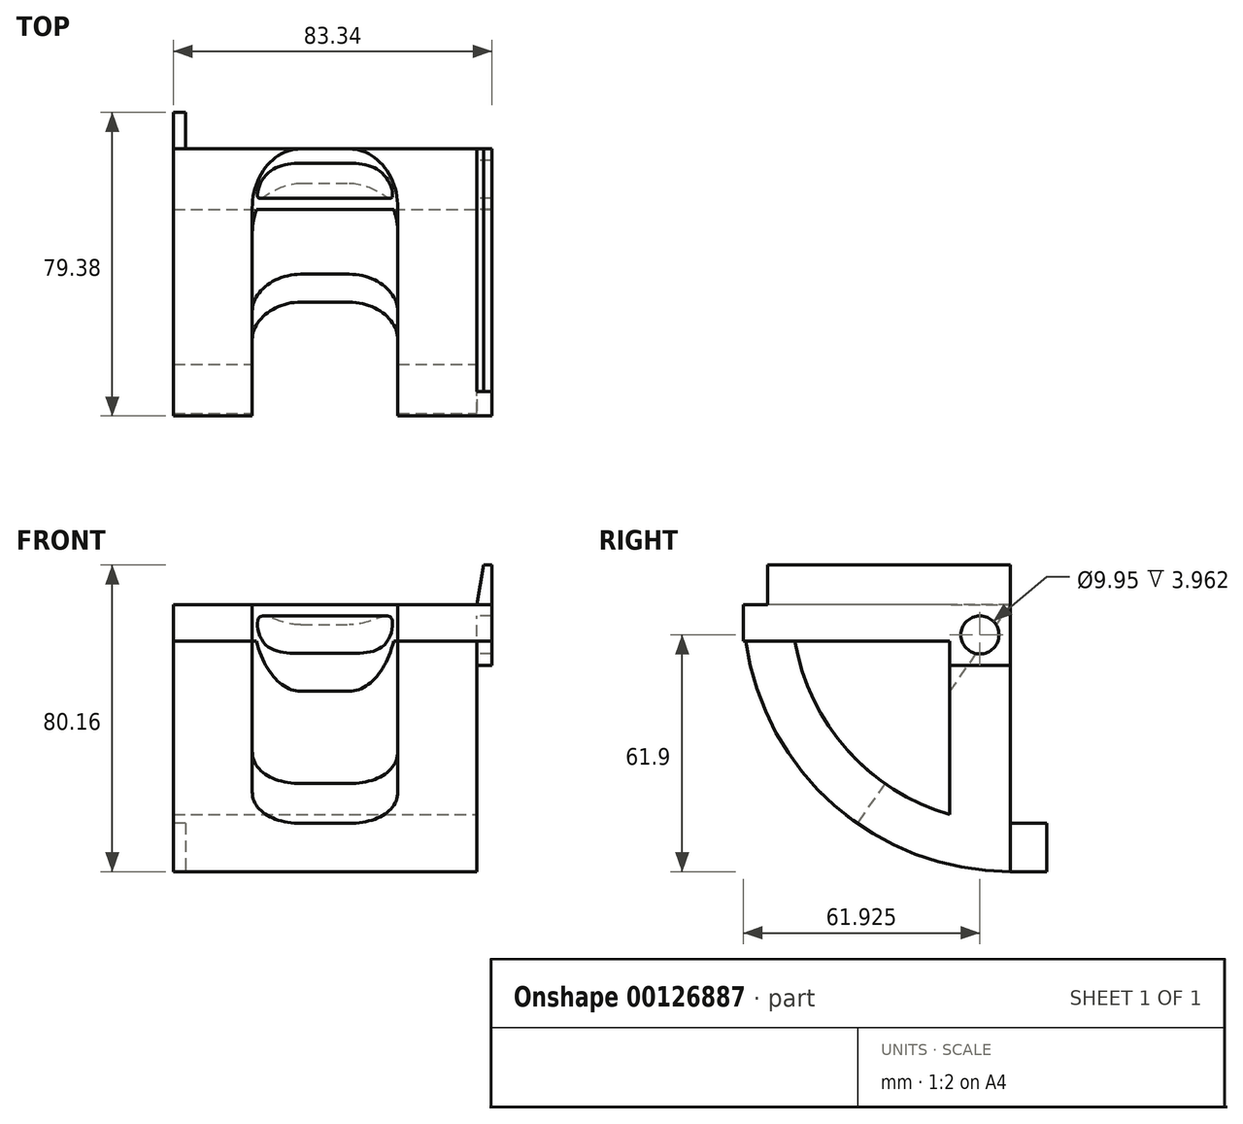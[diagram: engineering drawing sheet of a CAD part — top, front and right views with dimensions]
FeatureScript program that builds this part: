
annotation { "Feature Type Name" : "Feature", "Feature Type Description" : "" }
export const myFeature = defineFeature(function(context is Context, id is Id, definition is map)
    precondition{}
    {
        {
            var Q0;
            Q0=qCreatedBy(makeId("Right.planeOp"),FACE);
            var sketch = newSketch(context, id + "F0", { "sketchPlane" : qUnion([Q0])});
            skLineSegment(sketch, "E0.bottom", {"start": v(0, 0) * mm, "end": v(-69.85, 0) * mm});
            skLineSegment(sketch, "E0.left", {"start": v(0, 0) * mm, "end": v(0, -69.85) * mm});
            skLineSegment(sketch, "E0.right", {"start": v(-69.85, 0) * mm, "end": v(-69.85, -9.53) * mm});
            skArc(sketch, "E1", {"start": v(-57.15, 0) * mm, "mid": v(-40.41, -40.41) * mm, "end": v(0, -57.15) * mm});
            skArc(sketch, "E2", {"start": v(-69.85, 0) * mm, "mid": v(-49.4, -49.4) * mm, "end": v(0, -69.85) * mm});
            skLineSegment(sketch, "E3.0", {"start": v(0, -9.52) * mm, "end": v(-69.85, -9.53) * mm});
            skLineSegment(sketch, "E4.0", {"start": v(-15.87, -9.52) * mm, "end": v(-15.87, -54.9) * mm});
            skSolve(sketch);
        }
        {
            var Q0;
            Q0 = qSketchRegion(id + "F0", true);
            extrude(context, id + "F1", {"entities" : qUnion([Q0]), "oppositeDirection" : true, "depth" : 79.38 * mm});
        }
        {
            var Q0;
            Q0=qCreatedBy(makeId("Right.planeOp"),FACE);
            cPlane(context, id + "F2", {"entities" : qUnion([Q0]), "cplaneType" : CPlaneType.OFFSET, "offset" : 39.69 * mm, "oppositeDirection" : true, "width" : 152.4 * mm, "height" : 152.4 * mm});
        }
        {
            var Q0;
            Q0=qCreatedBy(id+"F2.planeOp",FACE);
            var sketch = newSketch(context, id + "F3", { "sketchPlane" : qUnion([Q0])});
            skLineSegment(sketch, "E5.0", {"start": v(0, 0) * mm, "end": v(-69.85, 0) * mm});
            skLineSegment(sketch, "E6.0", {"start": v(0, 0) * mm, "end": v(0, -69.85) * mm, "construction": true});
            skLineSegment(sketch, "E7", {"start": v(0, 0) * mm, "end": v(-40.06, -57.22) * mm});
            skPoint(sketch, "E8", {"position": v(-7.92, -7.95) * mm});
            skCircle(sketch, "E9", {"center": v(-7.92, -7.95) * mm, "radius": 4.97 * mm});
            skArc(sketch, "E10.0", {"start": v(-69.2, -9.53) * mm, "mid": v(-59.6, -36.41) * mm, "end": v(-40.06, -57.22) * mm});
            skArc(sketch, "E11", {"start": v(-40.06, -57.22) * mm, "mid": v(-21, -66.62) * mm, "end": v(0, -69.85) * mm});
            skLineSegment(sketch, "E12.0", {"start": v(-69.2, -9.53) * mm, "end": v(-69.85, -9.53) * mm});
            skLineSegment(sketch, "E13", {"start": v(-69.85, 0) * mm, "end": v(-69.85, -9.53) * mm});
            skPoint(sketch, "E14", {"position": v(-38.1, 0) * mm});
            skArc(sketch, "E15", {"start": v(-38.1, 0) * mm, "mid": v(-33.8, -17.6) * mm, "end": v(-21.85, -31.2) * mm});
            skSolve(sketch);
        }
        {
            var Q0;
            {var subQ0=sQuery(id+"F3.wireOp",EDGE,"E10.0");Q0=makeQuery(id+"F3.imprint","IMPRINT",FACE,{"disambiguationData":[TD([[makeQuery(id+"F3.imprint","IMPRINT",EDGE,{"derivedFrom":subQ0}),1.0]])]});}
            var Q1;
            {var subQ0=sQuery(id+"F3.wireOp",EDGE,"E9");var subQ1=sQuery(id+"F3.wireOp",EDGE,"E7");var subQ2=makeQuery(id+"F3.imprint","INTERSECT",VERTEX,{"disambiguationData":[OD(0.0)],"derivedFrom":[subQ1,subQ0]});Q1=makeQuery(id+"F3.imprint","IMPRINT",FACE,{"disambiguationData":[TD([[makeQuery(id+"F3.imprint","IMPRINT",EDGE,{"disambiguationData":[TD([[subQ2,-1.0]])],"derivedFrom":subQ1}),1.0]])]});}
            var Q2;
            {var subQ0=sQuery(id+"F3.wireOp",EDGE,"E9");var subQ1=sQuery(id+"F3.wireOp",EDGE,"E7");var subQ2=makeQuery(id+"F3.imprint","INTERSECT",VERTEX,{"disambiguationData":[OD(0.0)],"derivedFrom":[subQ1,subQ0]});Q2=makeQuery(id+"F3.imprint","IMPRINT",FACE,{"disambiguationData":[TD([[makeQuery(id+"F3.imprint","IMPRINT",EDGE,{"disambiguationData":[TD([[subQ2,-1.0]])],"derivedFrom":subQ1}),-1.0]])]});}
            extrude(context, id + "F4", {"entities" : qUnion([Q0, Q1, Q2]), "operationType" : NewBodyOperationType.REMOVE, "oppositeDirection" : true, "depth" : 19.05 * mm, "hasSecondDirection" : true, "secondDirectionOppositeDirection" : false, "secondDirectionDepth" : 19.05 * mm});
        }
        {
            var Q0;
            Q0=makeQuery(id+"F4.boolean.opBoolean","COPY",EDGE,{"derivedFrom":makeQuery(id+"F4.opExtrude","CAP_EDGE",EDGE,{"disambiguationData":[OSD([sQuery(id+"F3.wireOp",EDGE,"E15")])],"isStart":false})});
            var Q1;
            Q1=makeQuery(id+"F4.boolean.opBoolean","COPY",EDGE,{"derivedFrom":makeQuery(id+"F4.opExtrude","CAP_EDGE",EDGE,{"disambiguationData":[OSD([sQuery(id+"F3.wireOp",EDGE,"E7")])],"isStart":false})});
            var Q2;
            Q2=makeQuery(id+"F4.boolean.opBoolean","COPY",EDGE,{"derivedFrom":makeQuery(id+"F4.opExtrude","CAP_EDGE",EDGE,{"disambiguationData":[OSD([sQuery(id+"F3.wireOp",EDGE,"E15")])],"isStart":true})});
            var Q3;
            Q3=makeQuery(id+"F4.boolean.opBoolean","COPY",EDGE,{"derivedFrom":makeQuery(id+"F4.opExtrude","CAP_EDGE",EDGE,{"disambiguationData":[OSD([sQuery(id+"F3.wireOp",EDGE,"E7")])],"isStart":true})});
            fillet(context, id + "F5", {"entities" : qUnion([Q0, Q1, Q2, Q3]), "radius" : 12.7 * mm, "tangentPropagation" : true, "allowEdgeOverflow" : false});
        }
        {
            var Q0;
            Q0=makeQuery(id+"F1.opExtrude","CAP_FACE",FACE,{"disambiguationData":[OSD([sQuery(id+"F0.wireOp",EDGE,"E0.bottom"),sQuery(id+"F0.wireOp",EDGE,"E0.left"),sQuery(id+"F0.wireOp",EDGE,"E0.right"),sQuery(id+"F0.wireOp",EDGE,"E1"),sQuery(id+"F0.wireOp",EDGE,"E2"),sQuery(id+"F0.wireOp",EDGE,"E3.0"),sQuery(id+"F0.wireOp",EDGE,"E4.0")])],"isStart":true});
            var sketch = newSketch(context, id + "F6", { "sketchPlane" : qUnion([Q0])});
            skCircle(sketch, "E16.0", {"center": v(-7.92, -7.95) * mm, "radius": 4.97 * mm});
            skLineSegment(sketch, "E17.bottom", {"start": v(0, 0) * mm, "end": v(-63.5, 0) * mm});
            skLineSegment(sketch, "E17.top", {"start": v(0, 10.31) * mm, "end": v(-63.5, 10.31) * mm});
            skLineSegment(sketch, "E17.left", {"start": v(0, 0) * mm, "end": v(0, 10.31) * mm});
            skLineSegment(sketch, "E17.right", {"start": v(-63.5, 0) * mm, "end": v(-63.5, 10.31) * mm});
            skLineSegment(sketch, "E18", {"start": v(-69.85, -9.53) * mm, "end": v(-15.87, -9.53) * mm});
            skLineSegment(sketch, "E19", {"start": v(-15.87, -15.88) * mm, "end": v(0, -15.88) * mm});
            skLineSegment(sketch, "E20", {"start": v(-69.85, -9.53) * mm, "end": v(-69.85, 0) * mm});
            skLineSegment(sketch, "E21", {"start": v(-69.85, 0) * mm, "end": v(-63.5, 0) * mm});
            skLineSegment(sketch, "E22.0", {"start": v(-15.87, -9.52) * mm, "end": v(-15.87, -54.9) * mm});
            skLineSegment(sketch, "E23", {"start": v(-15.87, -9.52) * mm, "end": v(-15.87, -15.88) * mm});
            skLineSegment(sketch, "E24", {"start": v(0, -15.88) * mm, "end": v(0, 10.31) * mm});
            skSolve(sketch);
        }
        {
            var Q0;
            Q0=makeQuery(id+"F1.opExtrude","CAP_FACE",FACE,{"disambiguationData":[OSD([sQuery(id+"F0.wireOp",EDGE,"E0.bottom"),sQuery(id+"F0.wireOp",EDGE,"E0.left"),sQuery(id+"F0.wireOp",EDGE,"E0.right"),sQuery(id+"F0.wireOp",EDGE,"E1"),sQuery(id+"F0.wireOp",EDGE,"E2"),sQuery(id+"F0.wireOp",EDGE,"E3.0"),sQuery(id+"F0.wireOp",EDGE,"E4.0")])],"isStart":false});
            var sketch = newSketch(context, id + "F7", { "sketchPlane" : qUnion([Q0])});
            skLineSegment(sketch, "E25.0", {"start": v(0, 0) * mm, "end": v(0, -69.85) * mm, "construction": true});
            skArc(sketch, "E26.0", {"start": v(69.2, -9.53) * mm, "mid": v(45.9, -52.65) * mm, "end": v(0, -69.85) * mm, "construction": true});
            skLineSegment(sketch, "E27.0", {"start": v(0, 0) * mm, "end": v(69.85, 0) * mm, "construction": true});
            skLineSegment(sketch, "E28.0", {"start": v(69.85, 0) * mm, "end": v(69.85, -9.53) * mm, "construction": true});
            skLineSegment(sketch, "E29.0", {"start": v(69.2, -9.53) * mm, "end": v(69.85, -9.53) * mm, "construction": true});
            skLineSegment(sketch, "E30.bottom", {"start": v(0, -69.85) * mm, "end": v(-9.53, -69.85) * mm});
            skLineSegment(sketch, "E30.top", {"start": v(0, -57.15) * mm, "end": v(-9.53, -57.15) * mm});
            skLineSegment(sketch, "E30.left", {"start": v(0, -69.85) * mm, "end": v(0, -57.15) * mm});
            skLineSegment(sketch, "E30.right", {"start": v(-9.53, -69.85) * mm, "end": v(-9.53, -57.15) * mm});
            skSolve(sketch);
        }
        {
            var Q0;
            Q0 = qSketchRegion(id + "F7", true);
            extrude(context, id + "F8", {"entities" : qUnion([Q0]), "operationType" : NewBodyOperationType.ADD, "oppositeDirection" : true, "depth" : 3.17 * mm});
        }
        {
            var Q0;
            Q0=makeQuery(id+"F6.imprint","IMPRINT",FACE,{"disambiguationData":[TD([[makeQuery(id+"F6.imprint","IMPRINT",EDGE,{"derivedFrom":sQuery(id+"F6.wireOp",EDGE,"E17.bottom")}),-1.0]])]});
            var Q1;
            Q1=makeQuery(id+"F6.imprint","IMPRINT",FACE,{"disambiguationData":[TD([[makeQuery(id+"F6.imprint","IMPRINT",EDGE,{"derivedFrom":sQuery(id+"F6.wireOp",EDGE,"E16.0")}),-1.0]])]});
            extrude(context, id + "F9", {"entities" : qUnion([Q0, Q1]), "operationType" : NewBodyOperationType.ADD, "depth" : 3.96 * mm});
        }
        {
            var Q0;
            Q0=makeQuery(id+"F9.opExtrude","CAP_EDGE",EDGE,{"disambiguationData":[OSD([sQuery(id+"F6.wireOp",EDGE,"E17.top")])],"isStart":true});
            chamfer(context, id + "F10", {"entities" : qUnion([Q0]), "chamferType" : ChamferType.OFFSET_ANGLE, "width" : 10.3 * mm, "oppositeDirection" : true, "angle" : 10 * degree, "tangentPropagation" : true});
        }
    });
